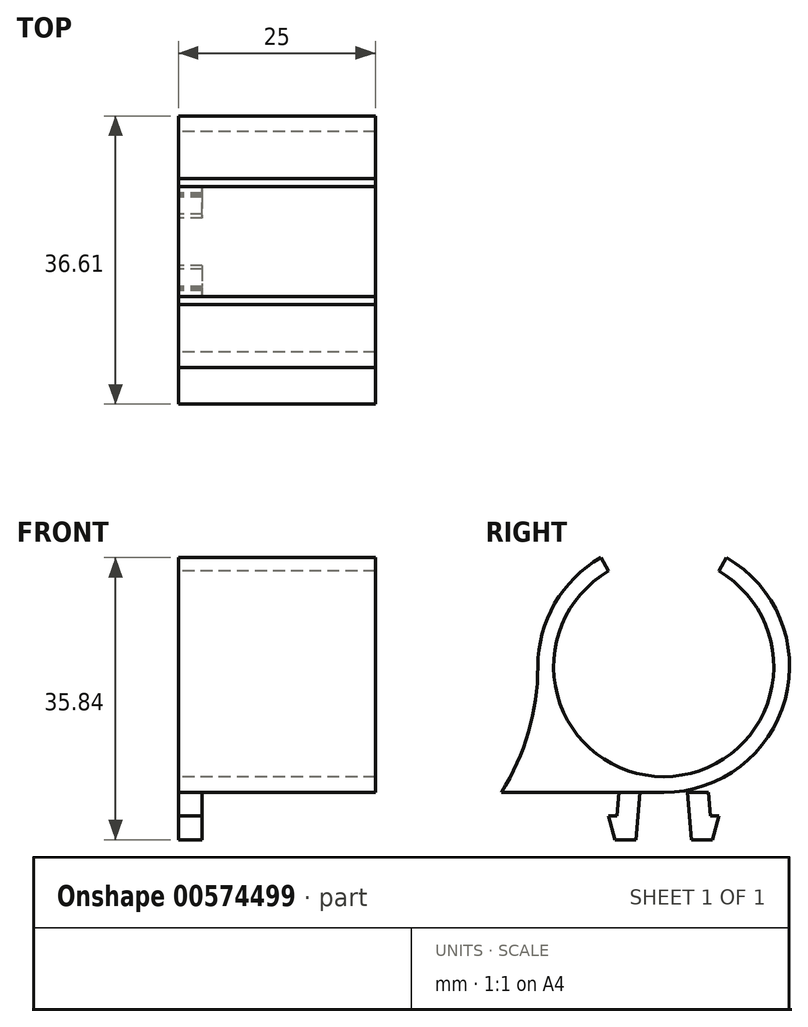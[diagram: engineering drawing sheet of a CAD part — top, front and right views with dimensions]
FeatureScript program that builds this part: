
annotation { "Feature Type Name" : "Feature", "Feature Type Description" : "" }
export const myFeature = defineFeature(function(context is Context, id is Id, definition is map)
    precondition{}
    {
        {
            var Q0;
            Q0=qCreatedBy(makeId("Right.planeOp"),FACE);
            var sketch = newSketch(context, id + "F0", { "sketchPlane" : qUnion([Q0])});
            skArc(sketch, "E0", {"start": v(-7, 28.1) * mm, "mid": v(0, 2) * mm, "end": v(7, 28.1) * mm});
            skArc(sketch, "E1", {"start": v(-8, 29.84) * mm, "mid": v(0, 0) * mm, "end": v(8, 29.84) * mm});
            skLineSegment(sketch, "E2", {"start": v(-7, 28.1) * mm, "end": v(-8, 29.84) * mm});
            skLineSegment(sketch, "E3.MirrorCS", {"start": v(7, 28.1) * mm, "end": v(8, 29.84) * mm});
            skLineSegment(sketch, "E4", {"start": v(0, 0) * mm, "end": v(-20.62, 0) * mm});
            skArc(sketch, "E5", {"start": v(-20.62, 0) * mm, "mid": v(-17.17, 7.67) * mm, "end": v(-16, 15.99) * mm});
            skPoint(sketch, "E6", {"position": v(-16, 16) * mm});
            skArc(sketch, "E7.MirrorCS", {"start": v(20.62, 0) * mm, "mid": v(17.17, 7.67) * mm, "end": v(16, 15.99) * mm});
            skLineSegment(sketch, "E8.MirrorCS", {"start": v(0, 0) * mm, "end": v(20.62, 0) * mm});
            skSolve(sketch);
        }
        {
            var Q0;
            Q0=makeQuery(id+"F0.imprint","IMPRINT",FACE,{"disambiguationData":[TD([[makeQuery(id+"F0.imprint","IMPRINT",EDGE,{"derivedFrom":sQuery(id+"F0.wireOp",EDGE,"E0")}),-1.0]])]});
            var Q1;
            {var subQ0=sQuery(id+"F0.wireOp",EDGE,"E4");Q1=makeQuery(id+"F0.imprint","IMPRINT",FACE,{"disambiguationData":[TD([[makeQuery(id+"F0.imprint","IMPRINT",EDGE,{"derivedFrom":subQ0}),-1.0]])]});}
            var Q2;
            {var subQ2=sQuery(id+"F0.wireOp",EDGE,"E7.MirrorCS");Q2=makeQuery(id+"F0.imprint","IMPRINT",FACE,{"disambiguationData":[TD([[makeQuery(id+"F0.imprint","IMPRINT",EDGE,{"derivedFrom":subQ2}),1.0]])]});}
            extrude(context, id + "F1", {"entities" : qUnion([Q0, Q1, Q2]), "depth" : 25 * mm, "offsetDistance" : 25 * mm});
        }
        {
            var Q0;
            Q0=qCreatedBy(makeId("Right.planeOp"),FACE);
            var sketch = newSketch(context, id + "F2", { "sketchPlane" : qUnion([Q0])});
            skLineSegment(sketch, "E9", {"start": v(3, 0) * mm, "end": v(3.5, -6) * mm});
            skLineSegment(sketch, "E10", {"start": v(3.5, -6) * mm, "end": v(6.2, -6) * mm});
            skLineSegment(sketch, "E11", {"start": v(6.2, -6) * mm, "end": v(7, -3) * mm});
            skLineSegment(sketch, "E12", {"start": v(7, -3) * mm, "end": v(5.95, -3) * mm});
            skLineSegment(sketch, "E13", {"start": v(5.95, -3) * mm, "end": v(5.7, 0) * mm});
            skLineSegment(sketch, "E14.MirrorCS", {"start": v(-7, -3) * mm, "end": v(-5.95, -3) * mm});
            skLineSegment(sketch, "E15.MirrorCS", {"start": v(-5.95, -3) * mm, "end": v(-5.7, 0) * mm});
            skLineSegment(sketch, "E16.MirrorCS", {"start": v(-3, 0) * mm, "end": v(-3.5, -6) * mm});
            skLineSegment(sketch, "E17.MirrorCS", {"start": v(-3.5, -6) * mm, "end": v(-6.2, -6) * mm});
            skLineSegment(sketch, "E18.MirrorCS", {"start": v(-6.2, -6) * mm, "end": v(-7, -3) * mm});
            skLineSegment(sketch, "E19", {"start": v(5.7, 0) * mm, "end": v(3, 0) * mm});
            skLineSegment(sketch, "E20", {"start": v(-3, 0) * mm, "end": v(-5.7, 0) * mm});
            skSolve(sketch);
        }
        {
            var Q0;
            Q0=makeQuery(id+"F2.imprint","IMPRINT",FACE,{"disambiguationData":[TD([[makeQuery(id+"F2.imprint","IMPRINT",EDGE,{"derivedFrom":sQuery(id+"F2.wireOp",EDGE,"E9")}),1.0]])]});
            var Q1;
            Q1=makeQuery(id+"F2.imprint","IMPRINT",FACE,{"disambiguationData":[TD([[makeQuery(id+"F2.imprint","IMPRINT",EDGE,{"derivedFrom":sQuery(id+"F2.wireOp",EDGE,"E14.MirrorCS")}),-1.0]])]});
            extrude(context, id + "F3", {"entities" : qUnion([Q0, Q1]), "operationType" : NewBodyOperationType.ADD, "depth" : 3 * mm, "offsetDistance" : 25 * mm});
        }
    });
